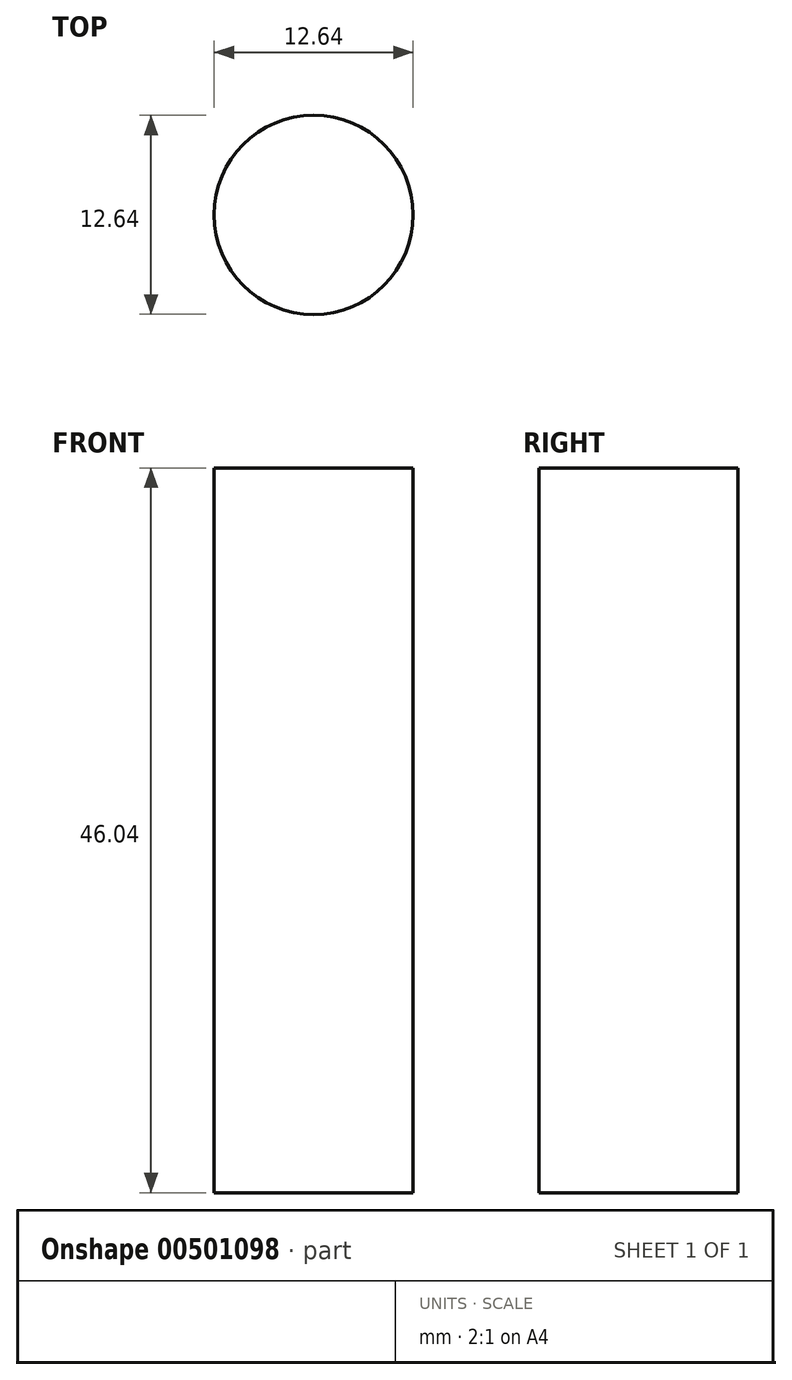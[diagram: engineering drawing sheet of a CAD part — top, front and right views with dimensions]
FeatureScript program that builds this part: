
annotation { "Feature Type Name" : "Feature", "Feature Type Description" : "" }
export const myFeature = defineFeature(function(context is Context, id is Id, definition is map)
    precondition{}
    {
        {
            var Q0;
            Q0=qCreatedBy(makeId("Top.planeOp"),FACE);
            var sketch = newSketch(context, id + "F0", { "sketchPlane" : qUnion([Q0])});
            skCircle(sketch, "E0", {"center": v(0, 0) * mm, "radius": 6.32 * mm});
            skLineSegment(sketch, "E1", {"start": v(-2, 6) * mm, "end": v(-2, 2) * mm});
            skLineSegment(sketch, "E2", {"start": v(-6, 2) * mm, "end": v(-2, 2) * mm});
            skLineSegment(sketch, "E3", {"start": v(-6, -2) * mm, "end": v(-2, -2) * mm});
            skLineSegment(sketch, "E4", {"start": v(-2, -2) * mm, "end": v(-2, -6) * mm});
            skLineSegment(sketch, "E5", {"start": v(2, -2) * mm, "end": v(2, -6) * mm});
            skLineSegment(sketch, "E6", {"start": v(6, -2) * mm, "end": v(2, -2) * mm});
            skLineSegment(sketch, "E7", {"start": v(2, 2) * mm, "end": v(2, 6) * mm});
            skLineSegment(sketch, "E8", {"start": v(2, 2) * mm, "end": v(6, 2) * mm});
            skLineSegment(sketch, "E9", {"start": v(6, 2) * mm, "end": v(6, -2) * mm});
            skLineSegment(sketch, "E10", {"start": v(-2, -6) * mm, "end": v(2, -6) * mm});
            skLineSegment(sketch, "E11", {"start": v(-6, 2) * mm, "end": v(-6, -2) * mm});
            skLineSegment(sketch, "E12", {"start": v(-2, 6) * mm, "end": v(2, 6) * mm});
            skSolve(sketch);
        }
        {
            var Q0;
            Q0 = qSketchRegion(id + "F0", true);
            extrude(context, id + "F1", {"entities" : qUnion([Q0]), "depth" : 46.04 * mm, "offsetDistance" : 25.4 * mm});
        }
    });
